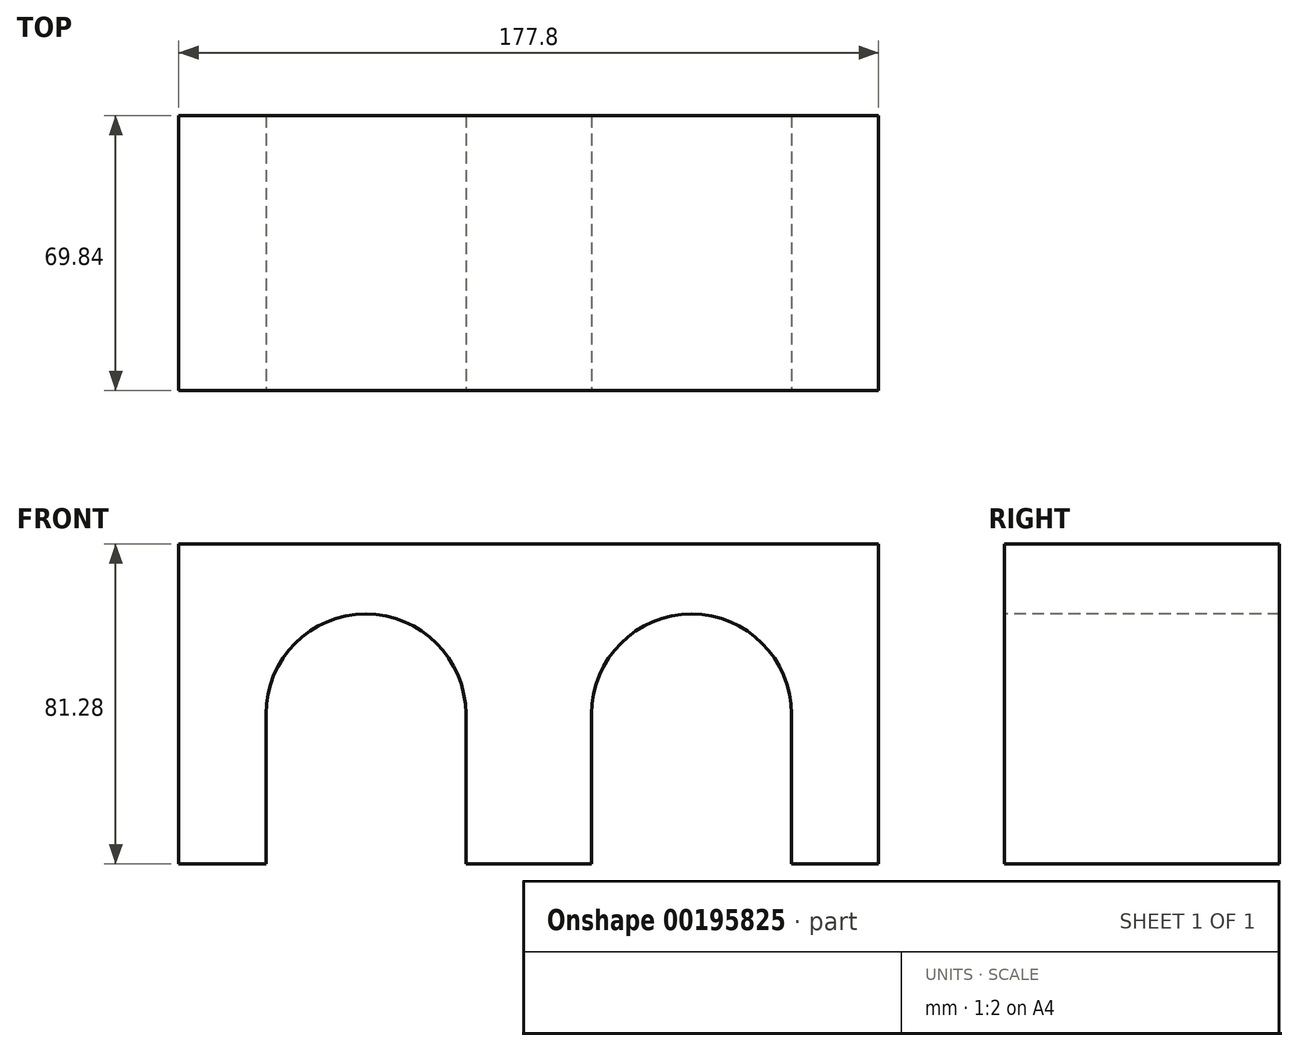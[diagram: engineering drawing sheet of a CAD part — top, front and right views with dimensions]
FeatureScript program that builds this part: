
annotation { "Feature Type Name" : "Feature", "Feature Type Description" : "" }
export const myFeature = defineFeature(function(context is Context, id is Id, definition is map)
    precondition{}
    {
        {
            var Q0;
            Q0=qCreatedBy(makeId("Top.planeOp"),FACE);
            var sketch = newSketch(context, id + "F0", { "sketchPlane" : qUnion([Q0])});
            skLineSegment(sketch, "E0.bottom", {"start": v(-88.9, 34.93) * mm, "end": v(88.9, 34.93) * mm});
            skLineSegment(sketch, "E0.top", {"start": v(-88.9, -34.93) * mm, "end": v(88.9, -34.93) * mm});
            skLineSegment(sketch, "E0.left", {"start": v(-88.9, 34.93) * mm, "end": v(-88.9, -34.93) * mm});
            skLineSegment(sketch, "E0.right", {"start": v(88.9, 34.93) * mm, "end": v(88.9, -34.93) * mm});
            skPoint(sketch, "E0.middle", {"position": v(0, 0) * mm});
            skSolve(sketch);
        }
        {
            var Q0;
            Q0=makeQuery(id+"F0.imprint","IMPRINT",FACE,{"disambiguationData":[TD([[makeQuery(id+"F0.imprint","IMPRINT",EDGE,{"derivedFrom":sQuery(id+"F0.wireOp",EDGE,"E0.bottom")}),-1.0]])]});
            extrude(context, id + "F1", {"entities" : qUnion([Q0]), "depth" : 81.28 * mm});
        }
        {
            var Q0;
            Q0=qCreatedBy(makeId("Front.planeOp"),FACE);
            cPlane(context, id + "F2", {"entities" : qUnion([Q0]), "cplaneType" : CPlaneType.OFFSET, "offset" : 34.92 * mm, "width" : 152.4 * mm, "height" : 152.4 * mm});
        }
        {
            var Q0;
            Q0=qCreatedBy(id+"F2.planeOp",FACE);
            var sketch = newSketch(context, id + "F3", { "sketchPlane" : qUnion([Q0])});
            skLineSegment(sketch, "E1.bottom", {"start": v(-66.77, 0) * mm, "end": v(-15.97, 0) * mm});
            skLineSegment(sketch, "E1.top", {"start": v(-66.77, 38.1) * mm, "end": v(-15.97, 38.1) * mm});
            skLineSegment(sketch, "E1.left", {"start": v(-66.77, 0) * mm, "end": v(-66.77, 38.1) * mm});
            skLineSegment(sketch, "E1.right", {"start": v(-15.97, 0) * mm, "end": v(-15.97, 38.1) * mm});
            skLineSegment(sketch, "E2.MirrorCS", {"start": v(66.77, 38.1) * mm, "end": v(15.97, 38.1) * mm});
            skLineSegment(sketch, "E3.MirrorCS", {"start": v(15.97, 0) * mm, "end": v(15.97, 38.1) * mm});
            skLineSegment(sketch, "E4.MirrorCS", {"start": v(66.77, 0) * mm, "end": v(66.77, 38.1) * mm});
            skLineSegment(sketch, "E5.MirrorCS", {"start": v(66.77, 0) * mm, "end": v(15.97, 0) * mm});
            skArc(sketch, "E6", {"start": v(-15.97, 38.1) * mm, "mid": v(-41.37, 63.5) * mm, "end": v(-66.77, 38.1) * mm});
            skArc(sketch, "E7", {"start": v(66.77, 38.1) * mm, "mid": v(41.37, 63.5) * mm, "end": v(15.97, 38.1) * mm});
            skSolve(sketch);
        }
        {
            var Q0;
            Q0=makeQuery(id+"F3.imprint","IMPRINT",FACE,{"disambiguationData":[TD([[makeQuery(id+"F3.imprint","IMPRINT",EDGE,{"derivedFrom":sQuery(id+"F3.wireOp",EDGE,"E1.top")}),1.0]])]});
            var Q1;
            Q1=makeQuery(id+"F3.imprint","IMPRINT",FACE,{"disambiguationData":[TD([[makeQuery(id+"F3.imprint","IMPRINT",EDGE,{"derivedFrom":sQuery(id+"F3.wireOp",EDGE,"E1.bottom")}),1.0]])]});
            extrude(context, id + "F4", {"entities" : qUnion([Q0, Q1]), "operationType" : NewBodyOperationType.REMOVE, "oppositeDirection" : true, "depth" : 69.85 * mm});
        }
        {
            var Q0;
            Q0=makeQuery(id+"F3.imprint","IMPRINT",FACE,{"disambiguationData":[TD([[makeQuery(id+"F3.imprint","IMPRINT",EDGE,{"derivedFrom":sQuery(id+"F3.wireOp",EDGE,"E2.MirrorCS")}),1.0]])]});
            var Q1;
            Q1=makeQuery(id+"F3.imprint","IMPRINT",FACE,{"disambiguationData":[TD([[makeQuery(id+"F3.imprint","IMPRINT",EDGE,{"derivedFrom":sQuery(id+"F3.wireOp",EDGE,"E2.MirrorCS")}),-1.0]])]});
            extrude(context, id + "F5", {"entities" : qUnion([Q0, Q1]), "operationType" : NewBodyOperationType.REMOVE, "oppositeDirection" : true, "depth" : 69.85 * mm});
        }
    });
